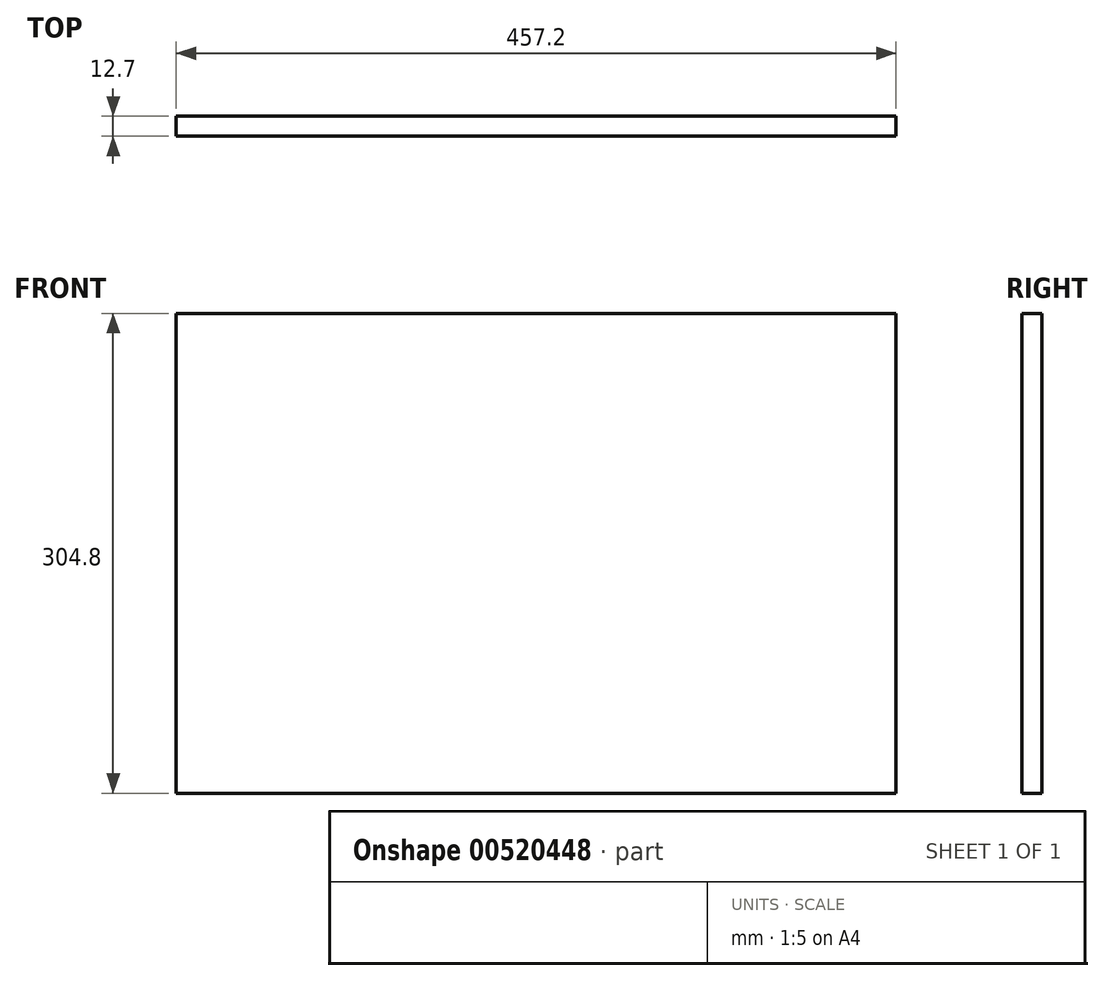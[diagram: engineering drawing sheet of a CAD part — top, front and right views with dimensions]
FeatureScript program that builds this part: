
annotation { "Feature Type Name" : "Feature", "Feature Type Description" : "" }
export const myFeature = defineFeature(function(context is Context, id is Id, definition is map)
    precondition{}
    {
        {
            var Q0;
            Q0=qCreatedBy(makeId("Front.planeOp"),FACE);
            var sketch = newSketch(context, id + "F0", { "sketchPlane" : qUnion([Q0])});
            skLineSegment(sketch, "E0.bottom", {"start": v(-220.18, 178.59) * mm, "end": v(237.02, 178.59) * mm});
            skLineSegment(sketch, "E0.top", {"start": v(-220.18, -126.21) * mm, "end": v(237.02, -126.21) * mm});
            skLineSegment(sketch, "E0.left", {"start": v(-220.18, 178.59) * mm, "end": v(-220.18, -126.21) * mm});
            skLineSegment(sketch, "E0.right", {"start": v(237.02, 178.59) * mm, "end": v(237.02, -126.21) * mm});
            skSolve(sketch);
        }
        {
            var Q0;
            Q0=makeQuery(id+"F0.imprint","IMPRINT",FACE,{"disambiguationData":[TD([[makeQuery(id+"F0.imprint","IMPRINT",EDGE,{"derivedFrom":sQuery(id+"F0.wireOp",EDGE,"E0.bottom")}),-1.0]])]});
            extrude(context, id + "F1", {"entities" : qUnion([Q0]), "depth" : 12.7 * mm, "offsetDistance" : 25.4 * mm});
        }
    });
